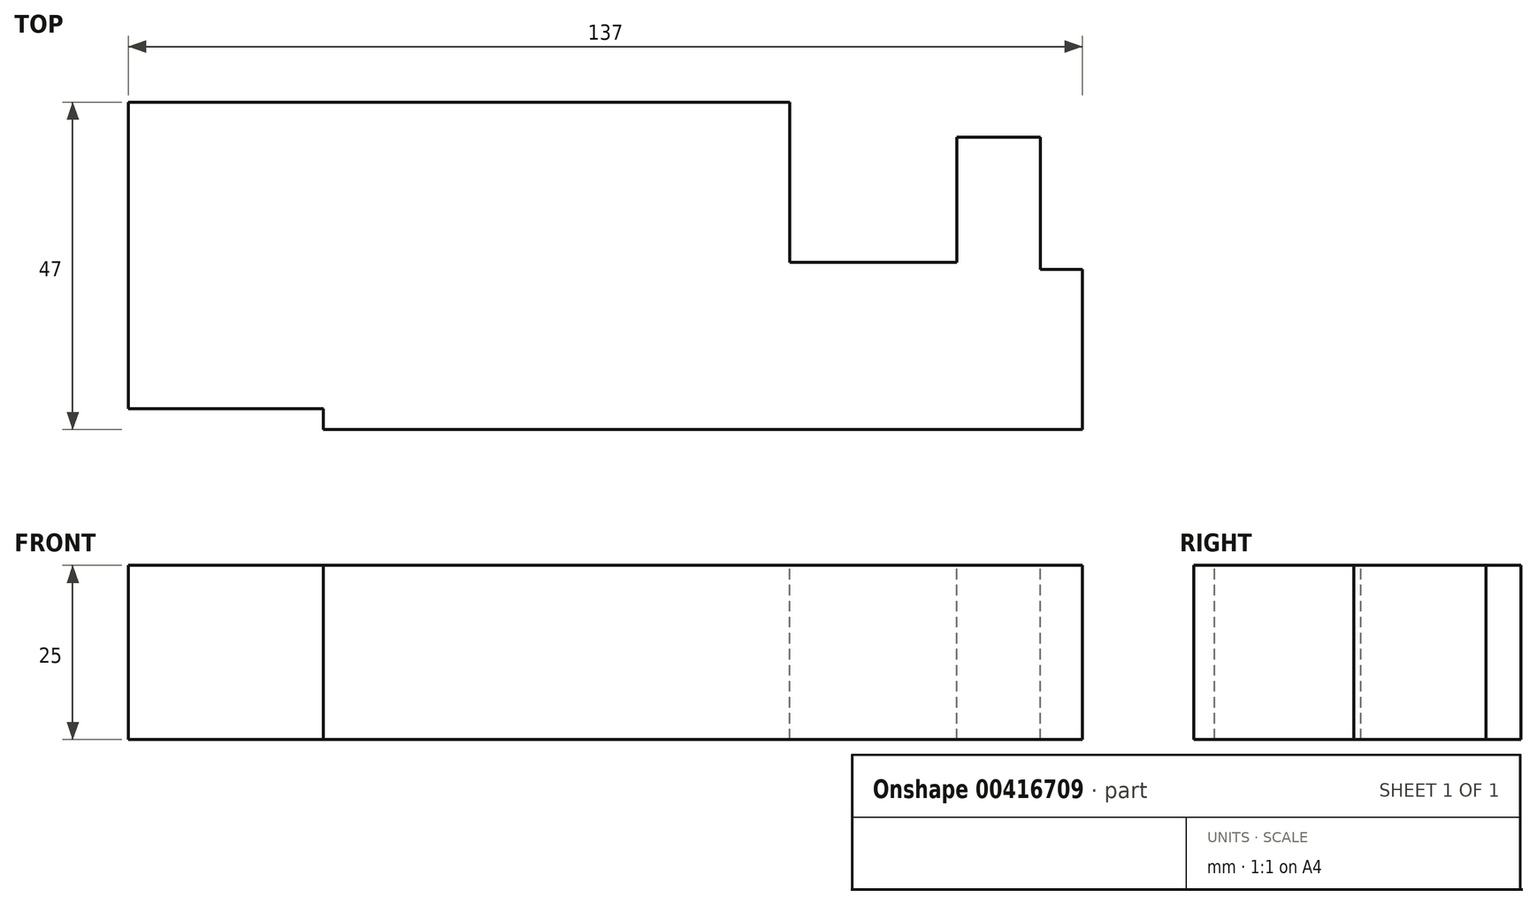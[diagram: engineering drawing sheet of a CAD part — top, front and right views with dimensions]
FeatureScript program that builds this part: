
annotation { "Feature Type Name" : "Feature", "Feature Type Description" : "" }
export const myFeature = defineFeature(function(context is Context, id is Id, definition is map)
    precondition{}
    {
        {
            var Q0;
            Q0=qCreatedBy(makeId("Top.planeOp"),FACE);
            var sketch = newSketch(context, id + "F0", { "sketchPlane" : qUnion([Q0])});
            skLineSegment(sketch, "E0.bottom", {"start": v(-129.46, 9.05) * mm, "end": v(-101.46, 9.05) * mm});
            skLineSegment(sketch, "E0.top", {"start": v(-129.46, -34.95) * mm, "end": v(-101.46, -34.95) * mm});
            skLineSegment(sketch, "E0.left", {"start": v(-129.46, 9.05) * mm, "end": v(-129.46, -34.95) * mm});
            skLineSegment(sketch, "E1.bottom", {"start": v(-101.46, 9.05) * mm, "end": v(-77.46, 9.05) * mm});
            skLineSegment(sketch, "E1.top", {"start": v(-101.46, -37.95) * mm, "end": v(-77.46, -37.95) * mm});
            skLineSegment(sketch, "E1.left", {"start": v(-101.46, -34.95) * mm, "end": v(-101.46, -37.95) * mm});
            skLineSegment(sketch, "E1.right", {"start": v(-77.46, 9.05) * mm, "end": v(-77.46, -37.95) * mm});
            skLineSegment(sketch, "E2.bottom", {"start": v(-77.46, 9.05) * mm, "end": v(-34.46, 9.05) * mm});
            skLineSegment(sketch, "E2.top", {"start": v(-77.46, -37.95) * mm, "end": v(-34.46, -37.95) * mm});
            skLineSegment(sketch, "E3.left", {"start": v(-34.46, 9.05) * mm, "end": v(-34.46, -13.95) * mm});
            skLineSegment(sketch, "E4", {"start": v(-34.46, -37.95) * mm, "end": v(7.54, -37.95) * mm});
            skLineSegment(sketch, "E5", {"start": v(7.54, -37.95) * mm, "end": v(7.54, -14.95) * mm});
            skLineSegment(sketch, "E6", {"start": v(7.54, -14.95) * mm, "end": v(1.54, -14.95) * mm});
            skLineSegment(sketch, "E7", {"start": v(1.54, -14.95) * mm, "end": v(1.54, 4.05) * mm});
            skLineSegment(sketch, "E8", {"start": v(1.54, 4.05) * mm, "end": v(-10.46, 4.05) * mm});
            skLineSegment(sketch, "E9", {"start": v(-10.46, 4.05) * mm, "end": v(-10.46, -13.95) * mm});
            skLineSegment(sketch, "E10", {"start": v(-10.46, -13.95) * mm, "end": v(-34.46, -13.95) * mm});
            skLineSegment(sketch, "E11", {"start": v(-101.46, 9.05) * mm, "end": v(-101.46, -34.95) * mm});
            skSolve(sketch);
        }
        {
            var Q0;
            Q0 = qSketchRegion(id + "F0", true);
            var Q1;
            Q1=sQuery(id+"F0.wireOp",EDGE,"E0.left");
            var Q2;
            Q2=sQuery(id+"F0.wireOp",EDGE,"E0.bottom");
            var Q3;
            Q3=sQuery(id+"F0.wireOp",EDGE,"E0.top");
            var Q4;
            Q4=sQuery(id+"F0.wireOp",EDGE,"E1.top");
            var Q5;
            Q5=sQuery(id+"F0.wireOp",EDGE,"E2.top");
            var Q6;
            Q6=sQuery(id+"F0.wireOp",EDGE,"E4");
            var Q7;
            Q7=sQuery(id+"F0.wireOp",EDGE,"E5");
            var Q8;
            Q8=sQuery(id+"F0.wireOp",EDGE,"E6");
            var Q9;
            Q9=sQuery(id+"F0.wireOp",EDGE,"E7");
            var Q10;
            Q10=sQuery(id+"F0.wireOp",EDGE,"E8");
            var Q11;
            Q11=sQuery(id+"F0.wireOp",EDGE,"E9");
            var Q12;
            Q12=sQuery(id+"F0.wireOp",EDGE,"E10");
            var Q13;
            Q13=sQuery(id+"F0.wireOp",EDGE,"E2.bottom");
            var Q14;
            Q14=sQuery(id+"F0.wireOp",EDGE,"E1.bottom");
            var Q15;
            Q15=sQuery(id+"F0.wireOp",EDGE,"E3.left");
            var Q16;
            Q16=sQuery(id+"F0.wireOp",EDGE,"E1.left");
            extrude(context, id + "F1", {"entities" : qUnion([Q0]), "bodyType" : ToolBodyType.SURFACE, "surfaceEntities" : qUnion([Q1, Q2, Q3, Q4, Q5, Q6, Q7, Q8, Q9, Q10, Q11, Q12, Q13, Q14, Q15, Q16]), "depth" : 25 * mm});
        }
    });
